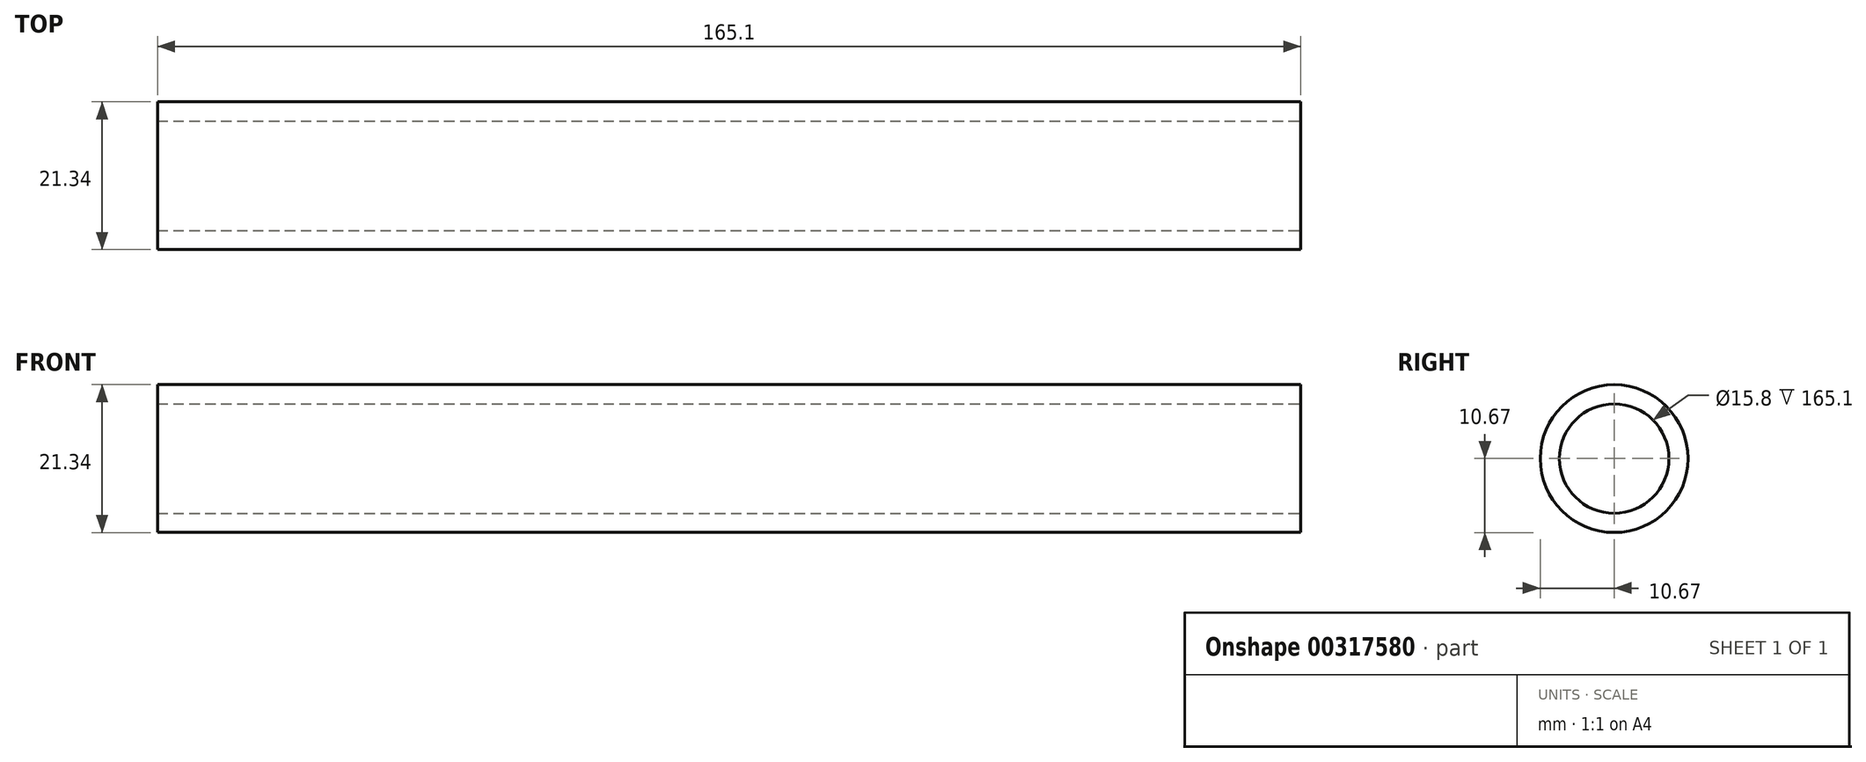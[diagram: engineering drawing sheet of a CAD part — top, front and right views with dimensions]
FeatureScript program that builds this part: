
annotation { "Feature Type Name" : "Feature", "Feature Type Description" : "" }
export const myFeature = defineFeature(function(context is Context, id is Id, definition is map)
    precondition{}
    {
        {
            var Q0;
            Q0=qCreatedBy(makeId("Right.planeOp"),FACE);
            var sketch = newSketch(context, id + "F0", { "sketchPlane" : qUnion([Q0])});
            skCircle(sketch, "E0", {"center": v(0, 0) * mm, "radius": 10.67 * mm});
            skSolve(sketch);
        }
        {
            var Q0;
            Q0=makeQuery(id+"F0.imprint","IMPRINT",FACE,{"disambiguationData":[TD([[makeQuery(id+"F0.imprint","IMPRINT",EDGE,{"derivedFrom":sQuery(id+"F0.wireOp",EDGE,"E0")}),1.0]])]});
            extrude(context, id + "F1", {"entities" : qUnion([Q0]), "endBound" : BoundingType.SYMMETRIC, "depth" : 165.1 * mm});
        }
        {
            var Q0;
            Q0=makeQuery(id+"F1.opExtrude","CAP_FACE",FACE,{"disambiguationData":[OSD([sQuery(id+"F0.wireOp",EDGE,"E0")])],"isStart":false});
            var sketch = newSketch(context, id + "F2", { "sketchPlane" : qUnion([Q0])});
            skCircle(sketch, "E1", {"center": v(0, 0) * mm, "radius": 7.9 * mm});
            skSolve(sketch);
        }
        {
            var Q0;
            Q0=sQuery(id+"F2.wireOp",VERTEX,"E1.center");
            var Q1;
            Q1=makeQuery(id+"F1.opExtrude","SWEPT_BODY",BODY,{"disambiguationData":[OSD([sQuery(id+"F0.wireOp",EDGE,"E0")])]});
            hole(context, id + "F3", {"style" : HoleStyle.SIMPLE, "endStyle" : HoleEndStyle.THROUGH, "holeDiameter" : 15.8 * mm, "tappedDepth" : 12.7 * mm, "tapClearance" : 3, "locations" : qUnion([Q0]), "scope" : qUnion([Q1])});
        }
    });
